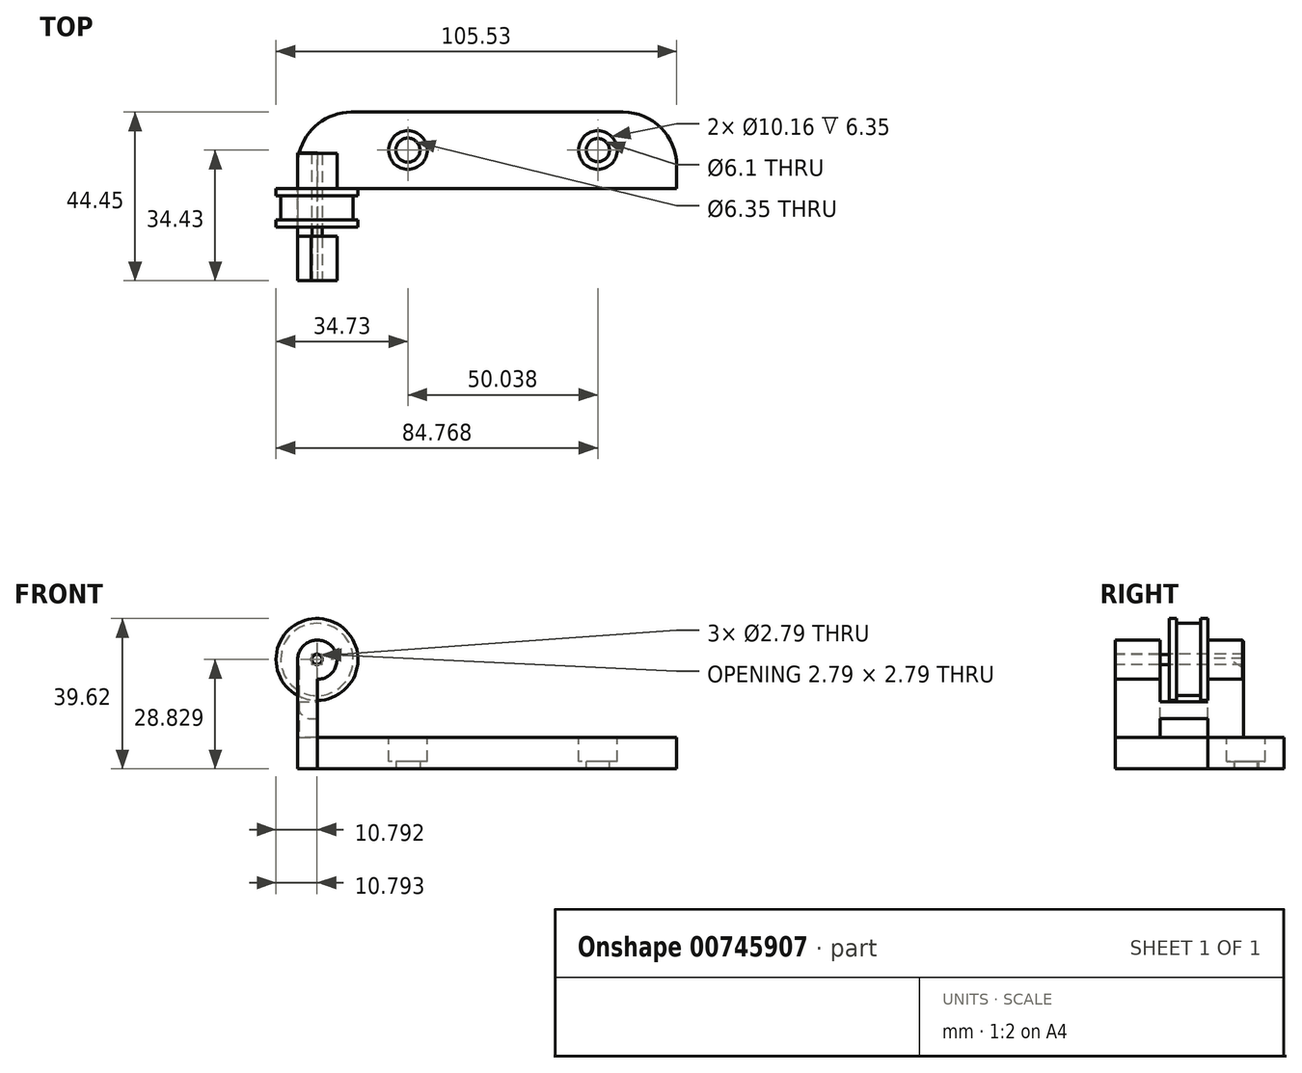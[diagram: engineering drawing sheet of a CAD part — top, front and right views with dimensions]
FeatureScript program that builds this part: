
annotation { "Feature Type Name" : "Feature", "Feature Type Description" : "" }
export const myFeature = defineFeature(function(context is Context, id is Id, definition is map)
    precondition{}
    {
        {
            var Q0;
            Q0=qCreatedBy(makeId("Top.planeOp"),FACE);
            var sketch = newSketch(context, id + "F0", { "sketchPlane" : qUnion([Q0])});
            skCircle(sketch, "E0", {"center": v(0, 0) * mm, "radius": 3.18 * mm});
            skSolve(sketch);
        }
        {
            var Q0;
            Q0=qCreatedBy(makeId("Top.planeOp"),FACE);
            var sketch = newSketch(context, id + "F1", { "sketchPlane" : qUnion([Q0])});
            skLineSegment(sketch, "E1.bottom", {"start": v(45.4, 10.02) * mm, "end": v(-29.02, 10.02) * mm});
            skLineSegment(sketch, "E1.top", {"start": v(45.4, -34.43) * mm, "end": v(-29.02, -34.43) * mm});
            skLineSegment(sketch, "E1.left", {"start": v(45.4, 10.02) * mm, "end": v(45.4, -34.43) * mm});
            skLineSegment(sketch, "E1.right", {"start": v(-29.02, 10.02) * mm, "end": v(-29.02, -34.43) * mm});
            skSolve(sketch);
        }
        {
            var Q0;
            Q0 = qSketchRegion(id + "F1", true);
            extrude(context, id + "F2", {"entities" : qUnion([Q0]), "depth" : 8.25 * mm, "offsetDistance" : 25.4 * mm});
        }
        {
            var Q0;
            Q0=makeQuery(id+"F2.opExtrude","CAP_FACE",FACE,{"disambiguationData":[OSD([sQuery(id+"F1.wireOp",EDGE,"E1.bottom"),sQuery(id+"F1.wireOp",EDGE,"E1.top"),sQuery(id+"F1.wireOp",EDGE,"E1.left"),sQuery(id+"F1.wireOp",EDGE,"E1.right")])],"isStart":false});
            var sketch = newSketch(context, id + "F3", { "sketchPlane" : qUnion([Q0])});
            skCircle(sketch, "E2", {"center": v(0, 0) * mm, "radius": 5.08 * mm});
            skSolve(sketch);
        }
        {
            var Q0;
            Q0 = qSketchRegion(id + "F0", true);
            extrude(context, id + "F4", {"entities" : qUnion([Q0]), "operationType" : NewBodyOperationType.REMOVE, "depth" : 36.83 * mm, "offsetDistance" : 25.4 * mm});
        }
        {
            var Q0;
            Q0 = qSketchRegion(id + "F3", true);
            extrude(context, id + "F5", {"entities" : qUnion([Q0]), "operationType" : NewBodyOperationType.REMOVE, "oppositeDirection" : true, "depth" : 6.35 * mm, "offsetDistance" : 25.4 * mm});
        }
        {
            var Q0;
            Q0=makeQuery(id+"F2.opExtrude","CAP_FACE",FACE,{"disambiguationData":[OSD([sQuery(id+"F1.wireOp",EDGE,"E1.bottom"),sQuery(id+"F1.wireOp",EDGE,"E1.top"),sQuery(id+"F1.wireOp",EDGE,"E1.left"),sQuery(id+"F1.wireOp",EDGE,"E1.right")])],"isStart":false});
            var sketch = newSketch(context, id + "F6", { "sketchPlane" : qUnion([Q0])});
            skLineSegment(sketch, "E3.bottom", {"start": v(-23.88, -10.16) * mm, "end": v(45.4, -10.16) * mm});
            skLineSegment(sketch, "E3.top", {"start": v(-23.88, -34.43) * mm, "end": v(45.4, -34.43) * mm});
            skLineSegment(sketch, "E3.left", {"start": v(-23.88, -10.16) * mm, "end": v(-23.88, -34.43) * mm});
            skLineSegment(sketch, "E3.right", {"start": v(45.4, -10.16) * mm, "end": v(45.4, -34.43) * mm});
            skSolve(sketch);
        }
        {
            var Q0;
            Q0 = qSketchRegion(id + "F6", true);
            extrude(context, id + "F7", {"entities" : qUnion([Q0]), "operationType" : NewBodyOperationType.REMOVE, "oppositeDirection" : true, "depth" : 25.4 * mm, "offsetDistance" : 25.4 * mm});
        }
        {
            var Q0;
            Q0=makeQuery(id+"F2.opExtrude","CAP_FACE",FACE,{"disambiguationData":[OSD([sQuery(id+"F1.wireOp",EDGE,"E1.bottom"),sQuery(id+"F1.wireOp",EDGE,"E1.top"),sQuery(id+"F1.wireOp",EDGE,"E1.left"),sQuery(id+"F1.wireOp",EDGE,"E1.right")])],"isStart":false});
            var sketch = newSketch(context, id + "F8", { "sketchPlane" : qUnion([Q0])});
            skLineSegment(sketch, "E4.bottom", {"start": v(-29.02, -34.43) * mm, "end": v(-23.83, -34.43) * mm});
            skLineSegment(sketch, "E4.top", {"start": v(-29.02, -0.68) * mm, "end": v(-23.83, -0.68) * mm});
            skLineSegment(sketch, "E4.left", {"start": v(-29.02, -34.43) * mm, "end": v(-29.02, -0.68) * mm});
            skLineSegment(sketch, "E4.right", {"start": v(-23.83, -34.43) * mm, "end": v(-23.83, -0.68) * mm});
            skSolve(sketch);
        }
        {
            var Q0;
            Q0 = qSketchRegion(id + "F8", true);
            extrude(context, id + "F9", {"entities" : qUnion([Q0]), "operationType" : NewBodyOperationType.ADD, "depth" : 25.4 * mm, "offsetDistance" : 25.4 * mm});
        }
        {
            var Q0;
            Q0=makeQuery(id+"F9.opExtrude","CAP_FACE",FACE,{"disambiguationData":[OSD([sQuery(id+"F8.wireOp",EDGE,"E4.bottom"),sQuery(id+"F8.wireOp",EDGE,"E4.top"),sQuery(id+"F8.wireOp",EDGE,"E4.left"),sQuery(id+"F8.wireOp",EDGE,"E4.right")])],"isStart":false});
            var sketch = newSketch(context, id + "F10", { "sketchPlane" : qUnion([Q0])});
            skLineSegment(sketch, "E5.bottom", {"start": v(-15.9, -10.08) * mm, "end": v(-29.25, -10.08) * mm});
            skLineSegment(sketch, "E5.top", {"start": v(-15.9, -22.73) * mm, "end": v(-29.25, -22.73) * mm});
            skLineSegment(sketch, "E5.left", {"start": v(-15.9, -10.08) * mm, "end": v(-15.9, -22.73) * mm});
            skLineSegment(sketch, "E5.right", {"start": v(-29.25, -10.08) * mm, "end": v(-29.25, -22.73) * mm});
            skSolve(sketch);
        }
        {
            var Q0;
            Q0=makeQuery(id+"F9.boolean.opBoolean","MERGE",FACE,{"derivedFrom":[makeQuery(id+"F2.opExtrude","SWEPT_FACE",FACE,{"disambiguationData":[OSD([sQuery(id+"F1.wireOp",EDGE,"E1.top")])]}),makeQuery(id+"F9.opExtrude","SWEPT_FACE",FACE,{"disambiguationData":[OSD([sQuery(id+"F8.wireOp",EDGE,"E4.bottom")])]})]});
            var sketch = newSketch(context, id + "F11", { "sketchPlane" : qUnion([Q0])});
            skCircle(sketch, "E6", {"center": v(-23.83, 28.77) * mm, "radius": 5.17 * mm});
            skSolve(sketch);
        }
        {
            var Q0;
            Q0 = qSketchRegion(id + "F11", true);
            extrude(context, id + "F12", {"entities" : qUnion([Q0]), "operationType" : NewBodyOperationType.ADD, "oppositeDirection" : true, "depth" : 33.53 * mm, "offsetDistance" : 25.4 * mm});
        }
        {
            var Q0;
            Q0 = qSketchRegion(id + "F10", true);
            extrude(context, id + "F13", {"entities" : qUnion([Q0]), "operationType" : NewBodyOperationType.REMOVE, "endBound" : BoundingType.SYMMETRIC, "oppositeDirection" : true, "depth" : 50.8 * mm, "offsetDistance" : 25.4 * mm});
        }
        {
            var Q0;
            {var subQ0=sQuery(id+"F8.wireOp",EDGE,"E4.left");var subQ1=sQuery(id+"F8.wireOp",EDGE,"E4.top");Q0=makeQuery(id+"F13.boolean.opBoolean","SPLIT",EDGE,{"disambiguationData":[TD([makeQuery(id+"F9.opExtrude","SWEPT_FACE",FACE,{"disambiguationData":[OSD([subQ1])]})])],"derivedFrom":makeQuery(id+"F9.opExtrude","CAP_EDGE",EDGE,{"disambiguationData":[OSD([subQ0])],"isStart":false})});}
            var Q1;
            {var subQ0=sQuery(id+"F8.wireOp",EDGE,"E4.left");Q1=makeQuery(id+"F13.boolean.opBoolean","SPLIT",EDGE,{"disambiguationData":[TD([makeQuery(id+"F2.opExtrude","SWEPT_FACE",FACE,{"disambiguationData":[OSD([sQuery(id+"F1.wireOp",EDGE,"E1.top")])]})])],"derivedFrom":makeQuery(id+"F9.opExtrude","CAP_EDGE",EDGE,{"disambiguationData":[OSD([subQ0])],"isStart":false})});}
            fillet(context, id + "F14", {"entities" : qUnion([Q0, Q1]), "radius" : 5.08 * mm, "tangentPropagation" : true, "allowEdgeOverflow" : false});
        }
        {
            var Q0;
            Q0=makeQuery(id+"F13.boolean.opBoolean","COPY",FACE,{"derivedFrom":makeQuery(id+"F13.opExtrude","SWEPT_FACE",FACE,{"disambiguationData":[OSD([sQuery(id+"F10.wireOp",EDGE,"E5.bottom")])]})});
            var sketch = newSketch(context, id + "F15", { "sketchPlane" : qUnion([Q0])});
            skLineSegment(sketch, "E7.bottom", {"start": v(-29.02, 17.66) * mm, "end": v(-23.83, 17.66) * mm});
            skLineSegment(sketch, "E7.top", {"start": v(-29.02, 13.19) * mm, "end": v(-23.83, 13.19) * mm});
            skLineSegment(sketch, "E7.left", {"start": v(-29.02, 17.66) * mm, "end": v(-29.02, 13.19) * mm});
            skLineSegment(sketch, "E7.right", {"start": v(-23.83, 17.66) * mm, "end": v(-23.83, 13.19) * mm});
            skSolve(sketch);
        }
        {
            var Q0;
            Q0 = qSketchRegion(id + "F15", true);
            extrude(context, id + "F16", {"entities" : qUnion([Q0]), "operationType" : NewBodyOperationType.ADD, "depth" : 21.34 * mm, "offsetDistance" : 25.4 * mm});
        }
        {
            var Q0;
            Q0=makeQuery(id+"F16.opExtrude","SWEPT_EDGE",EDGE,{"disambiguationData":[OSD([sQuery(id+"F1.wireOp",EDGE,"E1.right"),sQuery(id+"F8.wireOp",EDGE,"E4.left"),sQuery(id+"F10.wireOp",EDGE,"E5.bottom"),sQuery(id+"F15.wireOp",EDGE,"E7.top"),sQuery(id+"F15.wireOp",EDGE,"E7.left")])]});
            fillet(context, id + "F17", {"entities" : qUnion([Q0]), "radius" : 3.62 * mm, "tangentPropagation" : true, "allowEdgeOverflow" : false});
        }
        {
            var Q0;
            Q0=makeQuery(id+"F12.boolean.opBoolean","MERGE",FACE,{"derivedFrom":[makeQuery(id+"F9.boolean.opBoolean","MERGE",FACE,{"derivedFrom":[makeQuery(id+"F2.opExtrude","SWEPT_FACE",FACE,{"disambiguationData":[OSD([sQuery(id+"F1.wireOp",EDGE,"E1.top")])]}),makeQuery(id+"F9.opExtrude","SWEPT_FACE",FACE,{"disambiguationData":[OSD([sQuery(id+"F8.wireOp",EDGE,"E4.bottom")])]})]}),makeQuery(id+"F12.opExtrude","CAP_FACE",FACE,{"disambiguationData":[OSD([sQuery(id+"F11.wireOp",EDGE,"E6")])],"isStart":true})]});
            var sketch = newSketch(context, id + "F18", { "sketchPlane" : qUnion([Q0])});
            skCircle(sketch, "E8", {"center": v(-23.94, 28.83) * mm, "radius": 1.4 * mm});
            skSolve(sketch);
        }
        {
            var Q0;
            Q0 = qSketchRegion(id + "F18", true);
            extrude(context, id + "F19", {"entities" : qUnion([Q0]), "operationType" : NewBodyOperationType.REMOVE, "oppositeDirection" : true, "depth" : 30.48 * mm, "offsetDistance" : 25.4 * mm});
        }
        {
            var Q0;
            Q0=makeQuery(id+"F12.boolean.opBoolean","MERGE",FACE,{"derivedFrom":[makeQuery(id+"F9.boolean.opBoolean","MERGE",FACE,{"derivedFrom":[makeQuery(id+"F2.opExtrude","SWEPT_FACE",FACE,{"disambiguationData":[OSD([sQuery(id+"F1.wireOp",EDGE,"E1.top")])]}),makeQuery(id+"F9.opExtrude","SWEPT_FACE",FACE,{"disambiguationData":[OSD([sQuery(id+"F8.wireOp",EDGE,"E4.bottom")])]})]}),makeQuery(id+"F12.opExtrude","CAP_FACE",FACE,{"disambiguationData":[OSD([sQuery(id+"F11.wireOp",EDGE,"E6")])],"isStart":true})]});
            var sketch = newSketch(context, id + "F20", { "sketchPlane" : qUnion([Q0])});
            skCircle(sketch, "E9", {"center": v(-23.94, 28.83) * mm, "radius": 1.33 * mm});
            skSolve(sketch);
        }
        {
            var Q0;
            Q0 = qSketchRegion(id + "F20", true);
            extrude(context, id + "F21", {"entities" : qUnion([Q0]), "oppositeDirection" : true, "depth" : 27.18 * mm, "offsetDistance" : 25.4 * mm});
        }
        {
            var Q0;
            {var subQ5=makeQuery(id+"F13.opExtrude","SWEPT_FACE",FACE,{"disambiguationData":[OSD([sQuery(id+"F10.wireOp",EDGE,"E5.bottom")])]});Q0=makeQuery(id+"F16.boolean.opBoolean","SPLIT",FACE,{"disambiguationData":[TD([makeQuery(id+"F12.opExtrude","SWEPT_FACE",FACE,{"disambiguationData":[OSD([sQuery(id+"F11.wireOp",EDGE,"E6")])]})])],"derivedFrom":makeQuery(id+"F13.boolean.opBoolean","COPY",FACE,{"derivedFrom":subQ5})});}
            var sketch = newSketch(context, id + "F22", { "sketchPlane" : qUnion([Q0])});
            skCircle(sketch, "E10", {"center": v(-23.94, 28.83) * mm, "radius": 10.8 * mm});
            skSolve(sketch);
        }
        {
            var Q0;
            Q0 = qSketchRegion(id + "F22", true);
            extrude(context, id + "F23", {"entities" : qUnion([Q0]), "depth" : 1.9 * mm, "offsetDistance" : 25.4 * mm});
        }
        {
            var Q0;
            Q0=makeQuery(id+"F23.opExtrude","CAP_FACE",FACE,{"disambiguationData":[OSD([sQuery(id+"F22.wireOp",EDGE,"E10")])],"isStart":false});
            var sketch = newSketch(context, id + "F24", { "sketchPlane" : qUnion([Q0])});
            skCircle(sketch, "E11", {"center": v(-23.94, 28.83) * mm, "radius": 9.53 * mm});
            skSolve(sketch);
        }
        {
            var Q0;
            Q0 = qSketchRegion(id + "F24", true);
            extrude(context, id + "F25", {"entities" : qUnion([Q0]), "operationType" : NewBodyOperationType.ADD, "depth" : 6.35 * mm, "offsetDistance" : 25.4 * mm});
        }
        {
            var Q0;
            Q0=makeQuery(id+"F25.opExtrude","CAP_FACE",FACE,{"disambiguationData":[OSD([sQuery(id+"F24.wireOp",EDGE,"E11")])],"isStart":false});
            var sketch = newSketch(context, id + "F26", { "sketchPlane" : qUnion([Q0])});
            skCircle(sketch, "E12", {"center": v(-23.94, 28.83) * mm, "radius": 10.8 * mm});
            skSolve(sketch);
        }
        {
            var Q0;
            Q0 = qSketchRegion(id + "F26", true);
            extrude(context, id + "F27", {"entities" : qUnion([Q0]), "operationType" : NewBodyOperationType.ADD, "depth" : 1.9 * mm, "offsetDistance" : 25.4 * mm});
        }
        {
            var Q0;
            Q0=makeQuery(id+"F27.opExtrude","CAP_FACE",FACE,{"disambiguationData":[OSD([sQuery(id+"F26.wireOp",EDGE,"E12")])],"isStart":false});
            var sketch = newSketch(context, id + "F28", { "sketchPlane" : qUnion([Q0])});
            skCircle(sketch, "E13", {"center": v(-23.94, 28.83) * mm, "radius": 1.4 * mm});
            skSolve(sketch);
        }
        {
            var Q0;
            Q0 = qSketchRegion(id + "F28", true);
            extrude(context, id + "F29", {"entities" : qUnion([Q0]), "operationType" : NewBodyOperationType.REMOVE, "oppositeDirection" : true, "depth" : 25.4 * mm, "offsetDistance" : 25.4 * mm});
        }
        {
            var Q0;
            Q0=makeQuery(id+"F2.opExtrude","SWEPT_FACE",FACE,{"disambiguationData":[OSD([sQuery(id+"F1.wireOp",EDGE,"E1.left")])]});
            extrude(context, id + "F30", {"entities" : qUnion([Q0]), "operationType" : NewBodyOperationType.ADD, "depth" : 25.4 * mm, "offsetDistance" : 25.4 * mm});
        }
        {
            var Q0;
            {var subQ0=sQuery(id+"F1.wireOp",EDGE,"E1.left");Q0=makeQuery(id+"F30.boolean.opBoolean","MERGE",FACE,{"derivedFrom":[makeQuery(id+"F13.boolean.opBoolean","MERGE",FACE,{"derivedFrom":[makeQuery(id+"F2.opExtrude","CAP_FACE",FACE,{"disambiguationData":[OSD([sQuery(id+"F1.wireOp",EDGE,"E1.bottom"),sQuery(id+"F1.wireOp",EDGE,"E1.top"),subQ0,sQuery(id+"F1.wireOp",EDGE,"E1.right")])],"isStart":false}),makeQuery(id+"F13.opExtrude","CAP_FACE",FACE,{"disambiguationData":[OSD([sQuery(id+"F10.wireOp",EDGE,"E5.bottom"),sQuery(id+"F10.wireOp",EDGE,"E5.top"),sQuery(id+"F10.wireOp",EDGE,"E5.left"),sQuery(id+"F10.wireOp",EDGE,"E5.right")])],"isStart":false})]}),makeQuery(id+"F30.opExtrude","SWEPT_FACE",FACE,{"disambiguationData":[OSD([subQ0]),TDD([makeQuery(id+"F2.opExtrude","CAP_EDGE",EDGE,{"disambiguationData":[OSD([subQ0])],"isStart":false})])]})]});}
            var sketch = newSketch(context, id + "F31", { "sketchPlane" : qUnion([Q0])});
            skCircle(sketch, "E14", {"center": v(50.04, 0) * mm, "radius": 3.05 * mm});
            skSolve(sketch);
        }
        {
            var Q0;
            Q0 = qSketchRegion(id + "F31", true);
            extrude(context, id + "F32", {"entities" : qUnion([Q0]), "operationType" : NewBodyOperationType.REMOVE, "oppositeDirection" : true, "depth" : 25.4 * mm, "offsetDistance" : 25.4 * mm});
        }
        {
            var Q0;
            {var subQ0=sQuery(id+"F1.wireOp",EDGE,"E1.left");Q0=makeQuery(id+"F30.boolean.opBoolean","MERGE",FACE,{"derivedFrom":[makeQuery(id+"F13.boolean.opBoolean","MERGE",FACE,{"derivedFrom":[makeQuery(id+"F2.opExtrude","CAP_FACE",FACE,{"disambiguationData":[OSD([sQuery(id+"F1.wireOp",EDGE,"E1.bottom"),sQuery(id+"F1.wireOp",EDGE,"E1.top"),subQ0,sQuery(id+"F1.wireOp",EDGE,"E1.right")])],"isStart":false}),makeQuery(id+"F13.opExtrude","CAP_FACE",FACE,{"disambiguationData":[OSD([sQuery(id+"F10.wireOp",EDGE,"E5.bottom"),sQuery(id+"F10.wireOp",EDGE,"E5.top"),sQuery(id+"F10.wireOp",EDGE,"E5.left"),sQuery(id+"F10.wireOp",EDGE,"E5.right")])],"isStart":false})]}),makeQuery(id+"F30.opExtrude","SWEPT_FACE",FACE,{"disambiguationData":[OSD([subQ0]),TDD([makeQuery(id+"F2.opExtrude","CAP_EDGE",EDGE,{"disambiguationData":[OSD([subQ0])],"isStart":false})])]})]});}
            var sketch = newSketch(context, id + "F33", { "sketchPlane" : qUnion([Q0])});
            skCircle(sketch, "E15", {"center": v(50.04, 0) * mm, "radius": 5.08 * mm});
            skSolve(sketch);
        }
        {
            var Q0;
            Q0 = qSketchRegion(id + "F33", true);
            extrude(context, id + "F34", {"entities" : qUnion([Q0]), "operationType" : NewBodyOperationType.REMOVE, "oppositeDirection" : true, "depth" : 6.35 * mm, "offsetDistance" : 25.4 * mm});
        }
        {
            var Q0;
            Q0=makeQuery(id+"F2.opExtrude","SWEPT_EDGE",EDGE,{"disambiguationData":[OSD([sQuery(id+"F1.wireOp",EDGE,"E1.bottom"),sQuery(id+"F1.wireOp",EDGE,"E1.right")])]});
            var Q1;
            Q1=makeQuery(id+"F30.opExtrude","CAP_EDGE",EDGE,{"disambiguationData":[OSD([sQuery(id+"F1.wireOp",EDGE,"E1.bottom"),sQuery(id+"F1.wireOp",EDGE,"E1.left")])],"isStart":false});
            fillet(context, id + "F35", {"entities" : qUnion([Q0, Q1]), "radius" : 14.1 * mm, "tangentPropagation" : true, "allowEdgeOverflow" : false});
        }
    });
